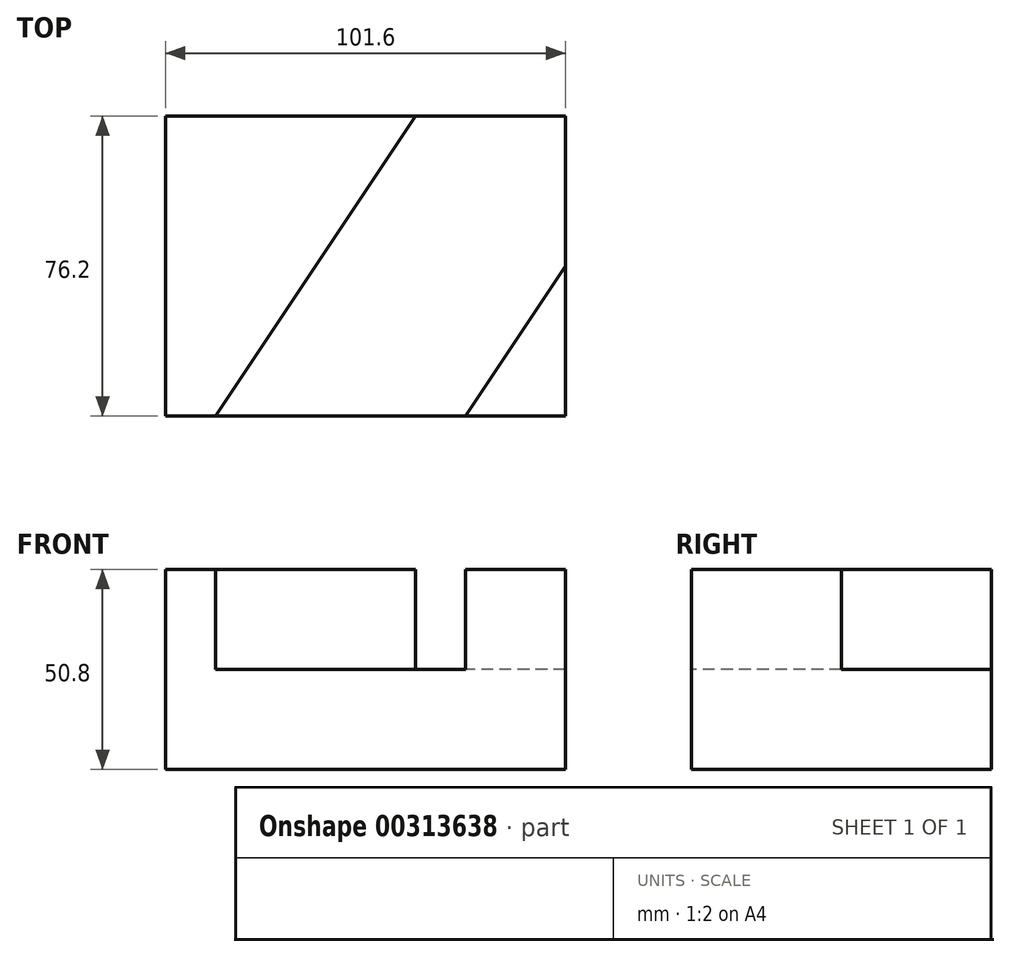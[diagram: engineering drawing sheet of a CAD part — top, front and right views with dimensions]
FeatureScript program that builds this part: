
annotation { "Feature Type Name" : "Feature", "Feature Type Description" : "" }
export const myFeature = defineFeature(function(context is Context, id is Id, definition is map)
    precondition{}
    {
        {
            var Q0;
            Q0=qCreatedBy(makeId("Top.planeOp"),FACE);
            var sketch = newSketch(context, id + "F0", { "sketchPlane" : qUnion([Q0])});
            skLineSegment(sketch, "E0", {"start": v(-42.77, -64.42) * mm, "end": v(58.83, -64.42) * mm});
            skLineSegment(sketch, "E1", {"start": v(58.83, -64.42) * mm, "end": v(58.83, 11.78) * mm});
            skLineSegment(sketch, "E2", {"start": v(58.83, 11.78) * mm, "end": v(-42.77, 11.78) * mm});
            skLineSegment(sketch, "E3", {"start": v(-42.77, 11.78) * mm, "end": v(-42.77, -64.42) * mm});
            skSolve(sketch);
        }
        {
            var Q0;
            Q0 = qSketchRegion(id + "F0", true);
            extrude(context, id + "F1", {"entities" : qUnion([Q0]), "depth" : 25.4 * mm});
        }
        {
            var Q0;
            Q0=makeQuery(id+"F1.opExtrude","CAP_FACE",FACE,{"disambiguationData":[OSD([sQuery(id+"F0.wireOp",EDGE,"E0"),sQuery(id+"F0.wireOp",EDGE,"E1"),sQuery(id+"F0.wireOp",EDGE,"E2"),sQuery(id+"F0.wireOp",EDGE,"E3")])],"isStart":false});
            var sketch = newSketch(context, id + "F2", { "sketchPlane" : qUnion([Q0])});
            skLineSegment(sketch, "E4", {"start": v(58.83, -64.42) * mm, "end": v(33.42, -64.42) * mm});
            skLineSegment(sketch, "E5", {"start": v(58.83, -64.42) * mm, "end": v(58.83, -26.32) * mm});
            skLineSegment(sketch, "E6", {"start": v(58.83, -26.32) * mm, "end": v(33.42, -64.42) * mm});
            skLineSegment(sketch, "E7", {"start": v(-42.77, -64.42) * mm, "end": v(-30.07, -64.42) * mm});
            skLineSegment(sketch, "E8", {"start": v(-42.77, -64.42) * mm, "end": v(-42.77, 11.78) * mm});
            skLineSegment(sketch, "E9", {"start": v(-42.77, 11.78) * mm, "end": v(20.73, 11.78) * mm});
            skLineSegment(sketch, "E10", {"start": v(20.73, 11.78) * mm, "end": v(-30.07, -64.42) * mm});
            skSolve(sketch);
        }
        {
            var Q0;
            Q0=makeQuery(id+"F2.imprint","IMPRINT",FACE,{"disambiguationData":[TD([[makeQuery(id+"F2.imprint","IMPRINT",EDGE,{"derivedFrom":sQuery(id+"F2.wireOp",EDGE,"E7")}),1.0]])]});
            var Q1;
            Q1=makeQuery(id+"F2.imprint","IMPRINT",FACE,{"disambiguationData":[TD([[makeQuery(id+"F2.imprint","IMPRINT",EDGE,{"derivedFrom":sQuery(id+"F2.wireOp",EDGE,"E4")}),1.0]])]});
            extrude(context, id + "F3", {"entities" : qUnion([Q0, Q1]), "operationType" : NewBodyOperationType.ADD, "depth" : 25.4 * mm});
        }
    });
